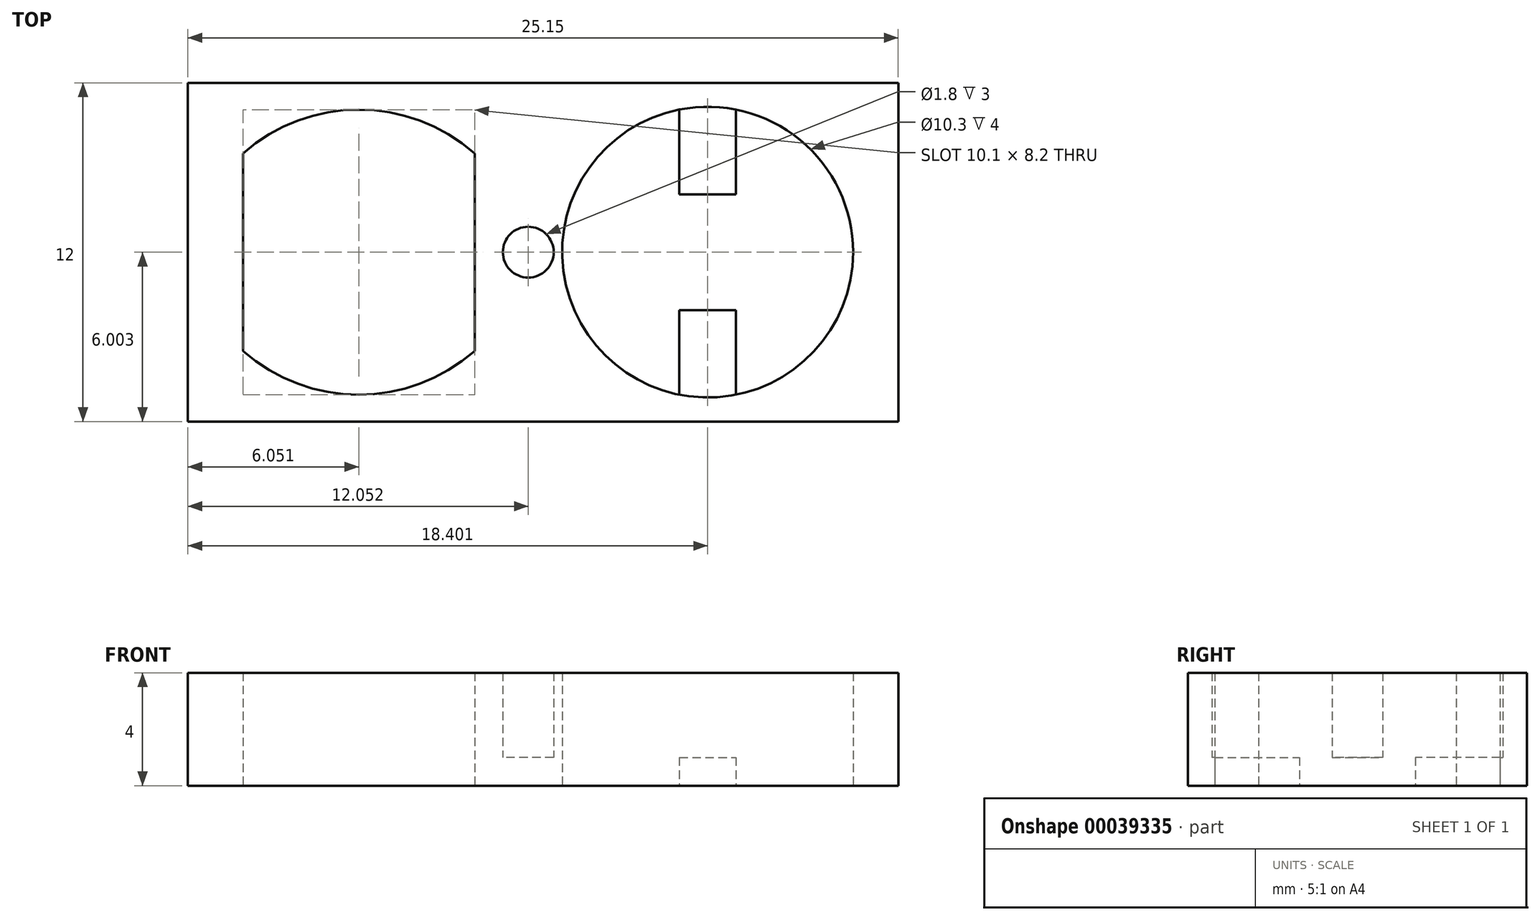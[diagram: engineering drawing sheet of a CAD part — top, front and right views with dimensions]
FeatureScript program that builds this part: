
annotation { "Feature Type Name" : "Feature", "Feature Type Description" : "" }
export const myFeature = defineFeature(function(context is Context, id is Id, definition is map)
    precondition{}
    {
        {
            var Q0;
            Q0=qCreatedBy(makeId("Top.planeOp"),FACE);
            var sketch = newSketch(context, id + "F0", { "sketchPlane" : qUnion([Q0])});
            skLineSegment(sketch, "E0", {"start": v(-11.3, 11.9) * mm, "end": v(-11.3, 8.4) * mm});
            skLineSegment(sketch, "E1", {"start": v(-13.26, 8.4) * mm, "end": v(11.9, 8.4) * mm, "construction": true});
            skPoint(sketch, "E2", {"position": v(-7.2, 11.9) * mm});
            skLineSegment(sketch, "E3", {"start": v(4.14, 3.35) * mm, "end": v(4.14, 6.35) * mm});
            skLineSegment(sketch, "E4", {"start": v(-11.3, 4.9) * mm, "end": v(-11.3, 8.4) * mm});
            skCircle(sketch, "E5", {"center": v(5.14, 8.4) * mm, "radius": 5.15 * mm});
            skPoint(sketch, "E6", {"position": v(-7.2, 4.9) * mm});
            skLineSegment(sketch, "E7", {"start": v(-3.1, 4.9) * mm, "end": v(-3.1, 8.4) * mm});
            skLineSegment(sketch, "E8", {"start": v(-3.1, 11.9) * mm, "end": v(-3.1, 8.4) * mm});
            skLineSegment(sketch, "E9", {"start": v(6.14, 6.35) * mm, "end": v(6.14, 3.35) * mm});
            skArc(sketch, "E10", {"start": v(-3.1, 11.9) * mm, "mid": v(-7.2, 13.45) * mm, "end": v(-11.3, 11.9) * mm});
            skCircle(sketch, "E11", {"center": v(-7.2, 8.4) * mm, "radius": 2 * mm});
            skLineSegment(sketch, "E12", {"start": v(4.14, 13.46) * mm, "end": v(4.14, 10.46) * mm});
            skArc(sketch, "E13", {"start": v(-11.3, 4.9) * mm, "mid": v(-7.2, 3.35) * mm, "end": v(-3.1, 4.9) * mm});
            skLineSegment(sketch, "E14.bottom", {"start": v(-13.26, 14.4) * mm, "end": v(11.9, 14.4) * mm});
            skPoint(sketch, "E15", {"position": v(-0.3, 8.4) * mm});
            skLineSegment(sketch, "E14.top", {"start": v(-13.26, 2.4) * mm, "end": v(11.9, 2.4) * mm});
            skPoint(sketch, "E16", {"position": v(0, 8.4) * mm});
            skLineSegment(sketch, "E17", {"start": v(6.14, 10.46) * mm, "end": v(6.14, 13.46) * mm});
            skLineSegment(sketch, "E18.bottom", {"start": v(-11.3, 11.9) * mm, "end": v(-3.1, 11.9) * mm, "construction": true});
            skLineSegment(sketch, "E14.left", {"start": v(-13.26, 14.4) * mm, "end": v(-13.26, 2.4) * mm});
            skPoint(sketch, "E19", {"position": v(-11.3, 8.4) * mm});
            skPoint(sketch, "E20", {"position": v(-2.1, 8.4) * mm});
            skLineSegment(sketch, "E18.top", {"start": v(-11.3, 4.9) * mm, "end": v(-3.1, 4.9) * mm, "construction": true});
            skLineSegment(sketch, "E14.right", {"start": v(11.9, 14.4) * mm, "end": v(11.9, 2.4) * mm});
            skPoint(sketch, "E21", {"position": v(-3.1, 8.4) * mm});
            skLineSegment(sketch, "E22", {"start": v(5.14, 13.55) * mm, "end": v(5.14, 3.25) * mm, "construction": true});
            skCircle(sketch, "E23", {"center": v(-1.2, 8.4) * mm, "radius": 0.9 * mm});
            skLineSegment(sketch, "E24", {"start": v(-7.2, 8.4) * mm, "end": v(-7.2, 13.45) * mm, "construction": true});
            skLineSegment(sketch, "E25", {"start": v(-7.2, 8.4) * mm, "end": v(-7.2, 3.35) * mm, "construction": true});
            skLineSegment(sketch, "E26", {"start": v(4.14, 6.35) * mm, "end": v(6.14, 6.35) * mm});
            skLineSegment(sketch, "E27", {"start": v(4.14, 10.46) * mm, "end": v(6.14, 10.46) * mm});
            skSolve(sketch);
        }
        {
            var Q0;
            Q0=makeQuery(id+"F0.imprint","IMPRINT",FACE,{"disambiguationData":[TD([[makeQuery(id+"F0.imprint","IMPRINT",EDGE,{"derivedFrom":sQuery(id+"F0.wireOp",EDGE,"E0")}),-1.0]])]});
            extrude(context, id + "F1", {"entities" : qUnion([Q0]), "depth" : 4 * mm});
        }
        {
            var Q0;
            {var subQ2=sQuery(id+"F0.wireOp",EDGE,"E3");Q0=makeQuery(id+"F0.imprint","IMPRINT",FACE,{"disambiguationData":[TD([[makeQuery(id+"F0.imprint","IMPRINT",EDGE,{"derivedFrom":subQ2}),-1.0]])]});}
            var Q1;
            {var subQ0=sQuery(id+"F0.wireOp",EDGE,"E12");Q1=makeQuery(id+"F0.imprint","IMPRINT",FACE,{"disambiguationData":[TD([[makeQuery(id+"F0.imprint","IMPRINT",EDGE,{"derivedFrom":subQ0}),1.0]])]});}
            var Q2;
            Q2=makeQuery(id+"F0.imprint","IMPRINT",FACE,{"disambiguationData":[TD([[makeQuery(id+"F0.imprint","IMPRINT",EDGE,{"derivedFrom":sQuery(id+"F0.wireOp",EDGE,"E23")}),1.0]])]});
            extrude(context, id + "F2", {"entities" : qUnion([Q0, Q1, Q2]), "operationType" : NewBodyOperationType.ADD, "depth" : 1 * mm});
        }
    });
